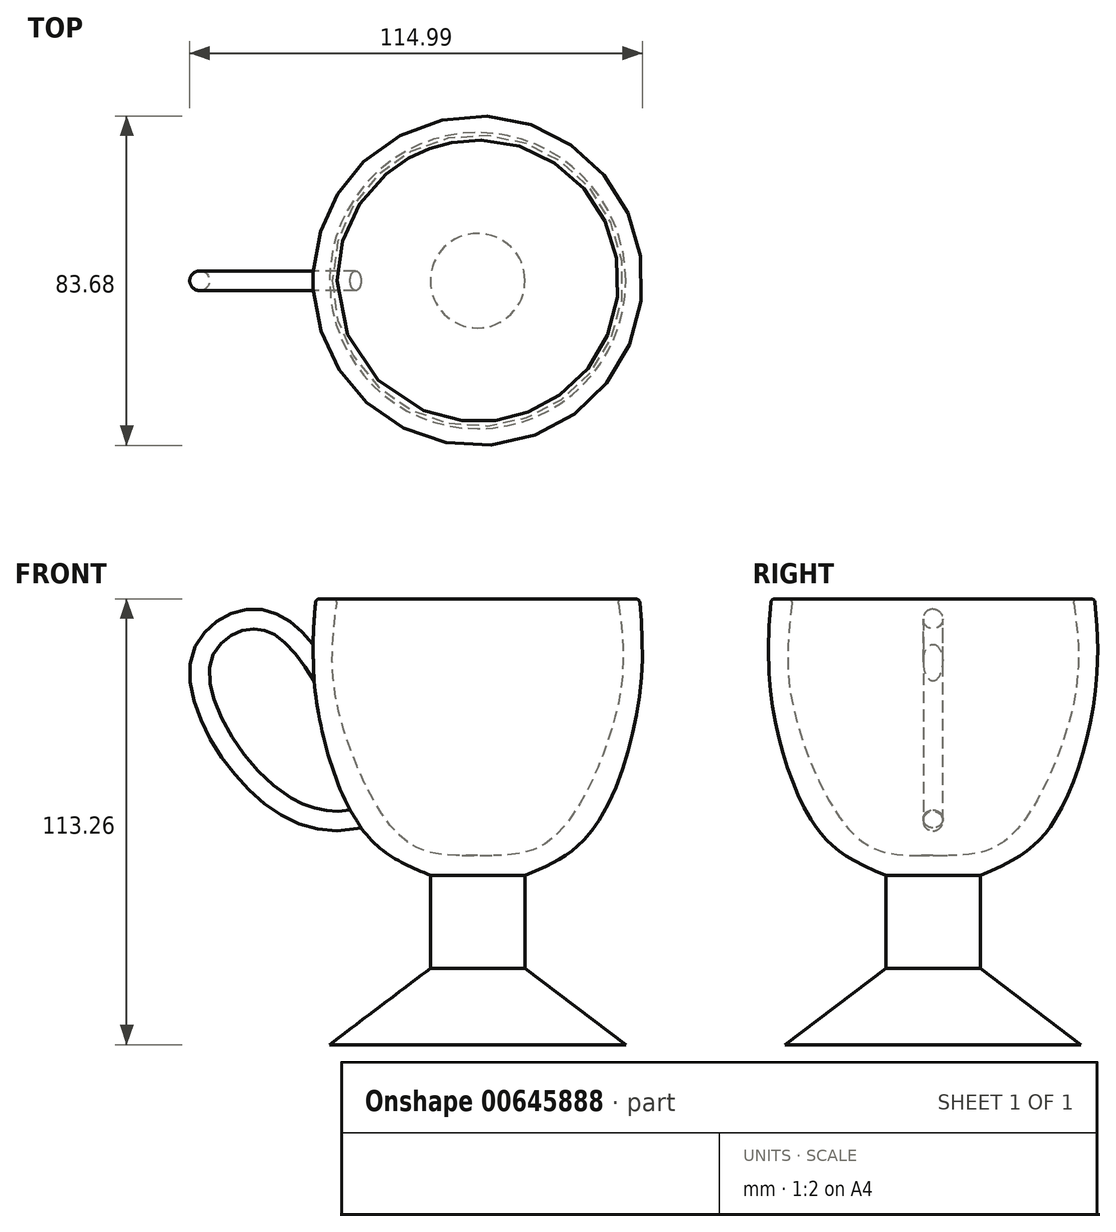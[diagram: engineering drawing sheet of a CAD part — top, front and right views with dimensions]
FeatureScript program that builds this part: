
annotation { "Feature Type Name" : "Feature", "Feature Type Description" : "" }
export const myFeature = defineFeature(function(context is Context, id is Id, definition is map)
    precondition{}
    {
        {
            var Q0;
            Q0=qCreatedBy(makeId("Front.planeOp"),FACE);
            var sketch = newSketch(context, id + "F0", { "sketchPlane" : qUnion([Q0])});
            skLineSegment(sketch, "E0", {"start": v(0, 0) * mm, "end": v(0, 113.26) * mm});
            skLineSegment(sketch, "E1", {"start": v(0, 0) * mm, "end": v(-37.62, 0) * mm});
            skLineSegment(sketch, "E2", {"start": v(-37.62, 0) * mm, "end": v(-12.02, 19.4) * mm});
            skLineSegment(sketch, "E3", {"start": v(-12.02, 19.4) * mm, "end": v(-12.02, 43.05) * mm});
            skFitSpline(sketch, "E4", {"points": [v(-12.02, 43.05) * mm, v(-28.7, 53.91) * mm, v(-41.11, 88.44) * mm, v(-41.11, 113.26) * mm], "startDerivative": vector(-61.97, 25.38) * mm, "endDerivative": vector(5.94, 70.93) * mm});
            skLineSegment(sketch, "E5", {"start": v(-41.11, 113.26) * mm, "end": v(0, 113.26) * mm});
            skFitSpline(sketch, "E6", {"points": [v(0, 48.13) * mm, v(-12.02, 48.83) * mm, v(-22.6, 56.2) * mm, v(-36.08, 88.48) * mm, v(-35.62, 113.26) * mm], "startDerivative": vector(-64.6, -1.58) * mm, "endDerivative": vector(11.56, 82.89) * mm});
            skFitSpline(sketch, "E7", {"points": [v(-41.82, 97.4) * mm, v(-56.47, 108.18) * mm, v(-70.05, 98.69) * mm, v(-58.8, 69.13) * mm, v(-31.09, 57.33) * mm], "startDerivative": vector(-57.79, 86.8) * mm, "endDerivative": vector(111.56, 24.3) * mm});
            skSolve(sketch);
        }
        {
            var Q0;
            Q0=sQuery(id+"F0.wireOp",EDGE,"E7");
            var Q1;
            Q1=sQuery(id+"F0.wireOp",VERTEX,"E7.0.internal");
            cPlane(context, id + "F1", {"entities" : qUnion([Q0, Q1]), "cplaneType" : CPlaneType.CURVE_POINT, "offset" : 25 * mm, "width" : 150 * mm, "height" : 150 * mm});
        }
        {
            var Q0;
            Q0=qCreatedBy(id+"F1.planeOp",FACE);
            var sketch = newSketch(context, id + "F2", { "sketchPlane" : qUnion([Q0])});
            skCircle(sketch, "E8", {"center": v(19.16, 0) * mm, "radius": 2.5 * mm});
            skSolve(sketch);
        }
        {
            var Q0;
            {var subQ0=sQuery(id+"F0.wireOp",EDGE,"E1");Q0=makeQuery(id+"F0.imprint","IMPRINT",FACE,{"disambiguationData":[TD([[makeQuery(id+"F0.imprint","IMPRINT",EDGE,{"derivedFrom":subQ0}),-1.0]])]});}
            var Q1;
            Q1=sQuery(id+"F0.wireOp",EDGE,"E0");
            revolve(context, id + "F3", {"entities" : qUnion([Q0]), "axis" : qUnion([Q1]), "revolveType" : RevolveType.FULL});
        }
        {
            var Q0;
            Q0=makeQuery(id+"F3.opRevolve","SWEPT_EDGE",EDGE,{"disambiguationData":[OSD([sQuery(id+"F0.wireOp",EDGE,"E5"),sQuery(id+"F0.wireOp",EDGE,"E6")])]});
            var Q1;
            Q1=makeQuery(id+"F3.opRevolve","SWEPT_EDGE",EDGE,{"disambiguationData":[OSD([sQuery(id+"F0.wireOp",EDGE,"E4"),sQuery(id+"F0.wireOp",EDGE,"E5")])]});
            fillet(context, id + "F4", {"entities" : qUnion([Q0, Q1]), "radius" : 1 * mm, "tangentPropagation" : true, "allowEdgeOverflow" : false});
        }
        {
            var Q0;
            Q0=makeQuery(id+"F2.imprint","IMPRINT",FACE,{"disambiguationData":[TD([[makeQuery(id+"F2.imprint","IMPRINT",EDGE,{"derivedFrom":sQuery(id+"F2.wireOp",EDGE,"E8")}),1.0]])]});
            var Q1;
            Q1=sQuery(id+"F0.wireOp",EDGE,"E7");
            sweep(context, id + "F5", {"operationType" : NewBodyOperationType.ADD, "profiles" : qUnion([Q0]), "path" : qUnion([Q1])});
        }
        {
            var Q0;
            Q0=makeQuery(id+"F5.opSweep","CAP_FACE",FACE,{"disambiguationData":[OSD([sQuery(id+"F0.wireOp",VERTEX,"E7.start"),sQuery(id+"F2.wireOp",EDGE,"E8")])],"isStart":true});
            var Q1;
            Q1=makeQuery(id+"F3.opRevolve","SWEPT_FACE",FACE,{"disambiguationData":[OSD([sQuery(id+"F0.wireOp",EDGE,"E4")])]});
            extrude(context, id + "F6", {"entities" : qUnion([Q0]), "operationType" : NewBodyOperationType.ADD, "endBound" : BoundingType.UP_TO_SURFACE, "depth" : 25 * mm, "endBoundEntityFace" : qUnion([Q1]), "offsetDistance" : 25 * mm});
        }
        {
            var Q0;
            Q0=makeQuery(id+"F5.opSweep","CAP_FACE",FACE,{"disambiguationData":[OSD([sQuery(id+"F0.wireOp",VERTEX,"E7.end"),sQuery(id+"F2.wireOp",EDGE,"E8")])],"isStart":false});
            var Q1;
            Q1=makeQuery(id+"F3.opRevolve","SWEPT_FACE",FACE,{"disambiguationData":[OSD([sQuery(id+"F0.wireOp",EDGE,"E4")])]});
            extrude(context, id + "F7", {"entities" : qUnion([Q0]), "operationType" : NewBodyOperationType.ADD, "endBound" : BoundingType.UP_TO_SURFACE, "depth" : 25 * mm, "endBoundEntityFace" : qUnion([Q1]), "offsetDistance" : 25 * mm});
        }
    });
